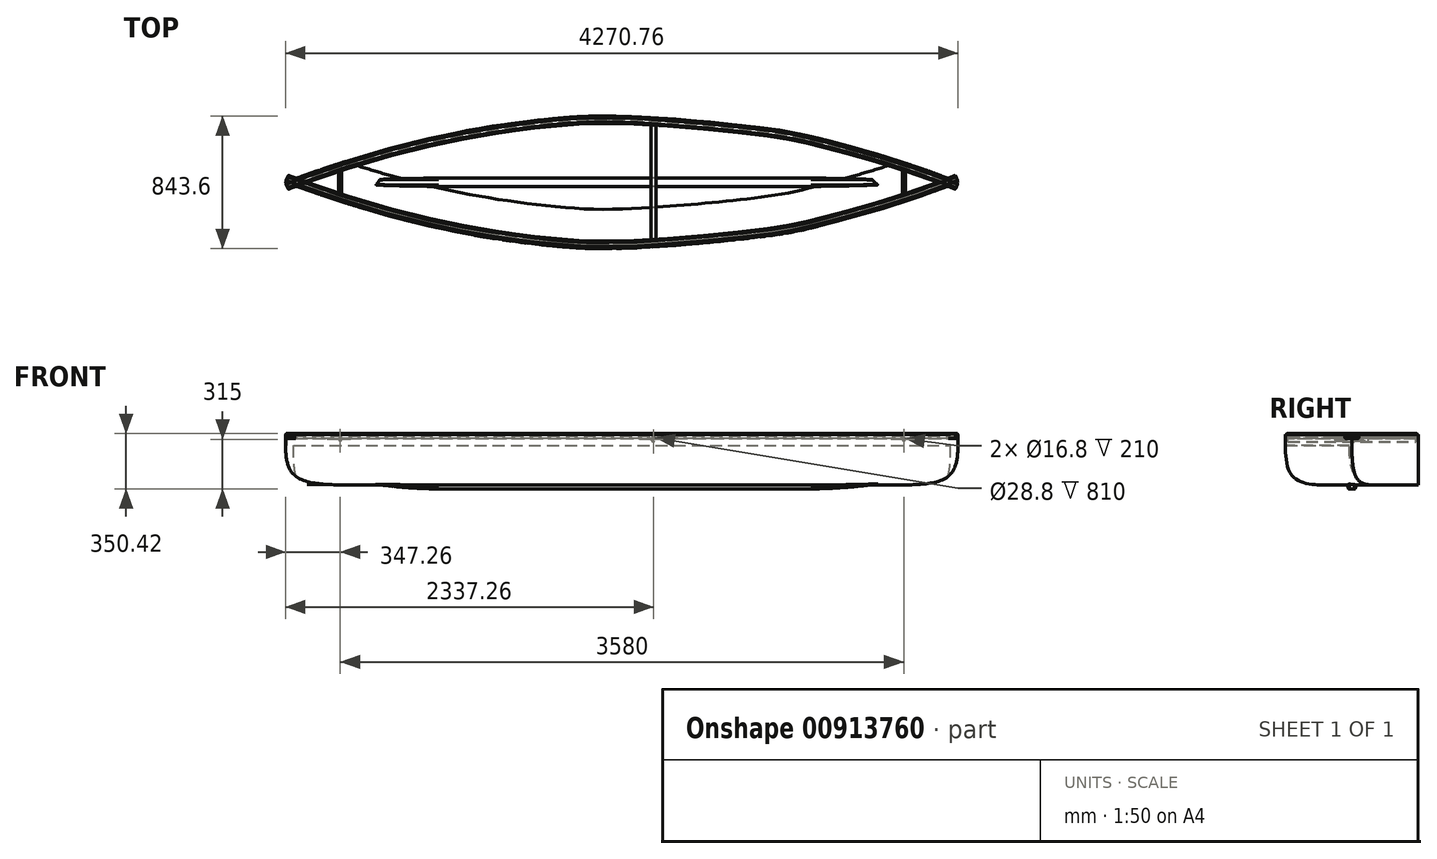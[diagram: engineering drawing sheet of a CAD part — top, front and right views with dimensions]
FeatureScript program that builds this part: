
annotation { "Feature Type Name" : "Feature", "Feature Type Description" : "" }
export const myFeature = defineFeature(function(context is Context, id is Id, definition is map)
    precondition{}
    {
        {
            var Q0;
            Q0=qCreatedBy(makeId("Top.planeOp"),FACE);
            var sketch = newSketch(context, id + "F0", { "sketchPlane" : qUnion([Q0])});
            skLineSegment(sketch, "E0", {"start": v(0, 0) * mm, "end": v(-3584.17, 0) * mm, "construction": true});
            skLineSegment(sketch, "E1", {"start": v(0, 0) * mm, "end": v(2133.5, 0) * mm, "construction": true});
            skFitSpline(sketch, "E2", {"points": [v(-2137.26, 0) * mm, v(-726.7, 370) * mm, v(-408.85, 407) * mm, v(0, 420) * mm, v(981, 333) * mm, v(1294.12, 267) * mm, v(2133.5, 0) * mm], "startDerivative": vector(8000.93, 3011.92) * mm, "endDerivative": vector(4907.5, -2014.73) * mm});
            skFitSpline(sketch, "E3.MirrorCS", {"points": [v(-2137.26, 0) * mm, v(-726.7, -370) * mm, v(-408.85, -407) * mm, v(0, -420) * mm, v(981, -333) * mm, v(1294.12, -267) * mm, v(2133.5, 0) * mm], "startDerivative": vector(8000.93, -3011.92) * mm, "endDerivative": vector(4907.5, 2014.73) * mm});
            skArc(sketch, "E4.filletArc", {"start": v(-2086.92, 18.76) * mm, "mid": v(-2100, 0) * mm, "end": v(-2086.92, -18.76) * mm});
            skArc(sketch, "E5.filletArc", {"start": v(2087.36, -18.6) * mm, "mid": v(2100, 0) * mm, "end": v(2087.36, 18.6) * mm});
            skSolve(sketch);
        }
        {
            var Q0;
            Q0 = qSketchRegion(id + "F0", true);
            extrude(context, id + "F1", {"entities" : qUnion([Q0]), "depth" : 320 * mm, "offsetDistance" : 25 * mm});
        }
        {
            var Q0;
            Q0=makeQuery(id+"F1.opExtrude","CAP_EDGE",EDGE,{"disambiguationData":[OSD([sQuery(id+"F0.wireOp",EDGE,"E3.MirrorCS")])],"isStart":true});
            fillet(context, id + "F2", {"entities" : qUnion([Q0]), "radius" : 250 * mm, "tangentPropagation" : true, "rho" : .6, "crossSection" : FilletCrossSection.CONIC, "allowEdgeOverflow" : false});
        }
        {
            var Q0;
            Q0=qCreatedBy(makeId("Right.planeOp"),FACE);
            var sketch = newSketch(context, id + "F3", { "sketchPlane" : qUnion([Q0])});
            skLineSegment(sketch, "E6", {"start": v(-27.5, 0) * mm, "end": v(-22.5, -25) * mm});
            skLineSegment(sketch, "E7", {"start": v(-22.5, -25) * mm, "end": v(22.5, -25) * mm});
            skLineSegment(sketch, "E8", {"start": v(22.5, -25) * mm, "end": v(27.5, 0) * mm});
            skLineSegment(sketch, "E9", {"start": v(27.5, 0) * mm, "end": v(-27.5, 0) * mm});
            skPoint(sketch, "E10.visualSharp", {"position": v(-22.5, -25) * mm});
            skPoint(sketch, "E11.visualSharp", {"position": v(22.5, -25) * mm});
            skSolve(sketch);
        }
        {
            var Q0;
            Q0 = qSketchRegion(id + "F3", true);
            extrude(context, id + "F4", {"entities" : qUnion([Q0]), "operationType" : NewBodyOperationType.ADD, "depth" : 1199.5 * mm, "offsetDistance" : 25 * mm, "hasSecondDirection" : true, "secondDirectionOppositeDirection" : true, "secondDirectionDepth" : 1166.8 * mm});
        }
        {
            var Q0;
            Q0=makeQuery(id+"F4.opExtrude","CAP_FACE",FACE,{"disambiguationData":[OSD([sQuery(id+"F3.wireOp",EDGE,"E6"),sQuery(id+"F3.wireOp",EDGE,"E7"),sQuery(id+"F3.wireOp",EDGE,"E8"),sQuery(id+"F3.wireOp",EDGE,"E9"),sQuery(id+"F3.wireOp",EDGE,"E10.filletArc"),sQuery(id+"F3.wireOp",EDGE,"E11.filletArc")])],"isStart":false});
            cPlane(context, id + "F5", {"entities" : qUnion([Q0]), "cplaneType" : CPlaneType.OFFSET, "offset" : 740 * mm, "width" : 150 * mm, "height" : 150 * mm});
        }
        {
            var Q0;
            Q0=qCreatedBy(id+"F5.planeOp",FACE);
            var sketch = newSketch(context, id + "F6", { "sketchPlane" : qUnion([Q0])});
            skLineSegment(sketch, "E12", {"start": v(-13, 52) * mm, "end": v(13, 52) * mm});
            skLineSegment(sketch, "E13", {"start": v(13, 52) * mm, "end": v(13.5, 57) * mm});
            skLineSegment(sketch, "E14", {"start": v(13.5, 57) * mm, "end": v(-13.5, 57) * mm});
            skLineSegment(sketch, "E15", {"start": v(-13.5, 57) * mm, "end": v(-13, 52) * mm});
            skSolve(sketch);
        }
        {
            var Q0;
            Q0=makeQuery(id+"F4.opExtrude","CAP_FACE",FACE,{"disambiguationData":[OSD([sQuery(id+"F3.wireOp",EDGE,"E6"),sQuery(id+"F3.wireOp",EDGE,"E7"),sQuery(id+"F3.wireOp",EDGE,"E8"),sQuery(id+"F3.wireOp",EDGE,"E9"),sQuery(id+"F3.wireOp",EDGE,"E10.filletArc"),sQuery(id+"F3.wireOp",EDGE,"E11.filletArc")])],"isStart":true});
            cPlane(context, id + "F7", {"entities" : qUnion([Q0]), "cplaneType" : CPlaneType.OFFSET, "offset" : 740 * mm, "width" : 150 * mm, "height" : 150 * mm});
        }
        {
            var Q0;
            Q0=makeQuery(id+"F2.opFillet","BLEND_EDGE",EDGE,{"disambiguationData":[OD(0.0)],"blendedFrom":[makeQuery(id+"F1.opExtrude","CAP_EDGE",EDGE,{"disambiguationData":[OSD([sQuery(id+"F0.wireOp",EDGE,"E2")])],"isStart":true}),makeQuery(id+"F1.opExtrude","CAP_EDGE",EDGE,{"disambiguationData":[OSD([sQuery(id+"F0.wireOp",EDGE,"E3.MirrorCS")])],"isStart":true})],"blendedInto":[]});
            var Q1;
            Q1=makeQuery(id+"F2.opFillet","BLEND_EDGE",EDGE,{"blendedFrom":[makeQuery(id+"F1.opExtrude","CAP_EDGE",EDGE,{"disambiguationData":[OSD([sQuery(id+"F0.wireOp",EDGE,"E3.MirrorCS")])],"isStart":true})],"blendedInto":[]});
            var Q3;
            Q3=makeQuery(id+"F4.opExtrude","CAP_FACE",FACE,{"disambiguationData":[OSD([sQuery(id+"F3.wireOp",EDGE,"E6"),sQuery(id+"F3.wireOp",EDGE,"E7"),sQuery(id+"F3.wireOp",EDGE,"E8"),sQuery(id+"F3.wireOp",EDGE,"E9")])],"isStart":false});
            var Q4;
            Q4 = qSketchRegion(id + "F6", true);
            var Q5;
            Q5=makeQuery(id+"F2.opFillet","BLEND_EDGE",EDGE,{"disambiguationData":[OD(0.0)],"blendedFrom":[makeQuery(id+"F1.opExtrude","CAP_EDGE",EDGE,{"disambiguationData":[OSD([sQuery(id+"F0.wireOp",EDGE,"E2")])],"isStart":true}),makeQuery(id+"F1.opExtrude","CAP_EDGE",EDGE,{"disambiguationData":[OSD([sQuery(id+"F0.wireOp",EDGE,"E3.MirrorCS")])],"isStart":true})],"blendedInto":[]});
            var Q6;
            Q6=makeQuery(id+"F2.opFillet","BLEND_EDGE",EDGE,{"blendedFrom":[makeQuery(id+"F1.opExtrude","CAP_EDGE",EDGE,{"disambiguationData":[OSD([sQuery(id+"F0.wireOp",EDGE,"E3.MirrorCS")])],"isStart":true})],"blendedInto":[]});
            var Q7;
            Q7=sQuery(id+"F6.wireOp",VERTEX,"E12.end");
            var Q8;
            Q8=makeQuery(id+"F4.opExtrude","CAP_VERTEX",VERTEX,{"disambiguationData":[OSD([sQuery(id+"F3.wireOp",EDGE,"E7"),sQuery(id+"F3.wireOp",EDGE,"E8")])],"isStart":false});
            loft(context, id + "F8", {"operationType" : NewBodyOperationType.ADD, "spine" : qUnion([Q0, Q1]), "startCondition" : LoftEndDerivativeType.MATCH_TANGENT, "startMagnitude" : 1, "sheetProfilesArray" : [{ "sheetProfileEntities" : qUnion([Q3]) }, { "sheetProfileEntities" : qUnion([Q4]) }], "guidesArray" : [{ "guideEntities" : qUnion([Q5]), "guideDerivativeType" : LoftGuideDerivativeType.DEFAULT, "guideDerivativeMagnitude" : 1 }, { "guideEntities" : qUnion([Q6]), "guideDerivativeType" : LoftGuideDerivativeType.DEFAULT, "guideDerivativeMagnitude" : 1 }], "matchConnections" : true, "connections" : [{ "connectionEntities" : qUnion([Q7, Q8]), "connectionEdgeQueries" : qUnion([]), "connectionEdgeParameters" : [] }]});
        }
        {
            var Q0;
            Q0=qCreatedBy(id+"F7.planeOp",FACE);
            var sketch = newSketch(context, id + "F9", { "sketchPlane" : qUnion([Q0])});
            skLineSegment(sketch, "E16", {"start": v(-14, 62) * mm, "end": v(14, 62) * mm});
            skLineSegment(sketch, "E17", {"start": v(14, 62) * mm, "end": v(13.5, 57) * mm});
            skLineSegment(sketch, "E18", {"start": v(13.5, 57) * mm, "end": v(-13.5, 57) * mm});
            skLineSegment(sketch, "E19", {"start": v(-13.5, 57) * mm, "end": v(-14, 62) * mm});
            skSolve(sketch);
        }
        {
            var Q1;
            Q1=makeQuery(id+"F9.imprint","IMPRINT",FACE,{"disambiguationData":[TD([[makeQuery(id+"F9.imprint","IMPRINT",EDGE,{"derivedFrom":sQuery(id+"F9.wireOp",EDGE,"E16")}),-1.0]])]});
            var Q2;
            Q2=makeQuery(id+"F4.opExtrude","CAP_FACE",FACE,{"disambiguationData":[OSD([sQuery(id+"F3.wireOp",EDGE,"E6"),sQuery(id+"F3.wireOp",EDGE,"E7"),sQuery(id+"F3.wireOp",EDGE,"E8"),sQuery(id+"F3.wireOp",EDGE,"E9"),sQuery(id+"F3.wireOp",EDGE,"E10.filletArc"),sQuery(id+"F3.wireOp",EDGE,"E11.filletArc")])],"isStart":true});
            loft(context, id + "F10", {"operationType" : NewBodyOperationType.ADD, "endCondition" : LoftEndDerivativeType.MATCH_TANGENT, "endMagnitude" : 1, "sheetProfilesArray" : [{ "sheetProfileEntities" : qUnion([Q1]) }, { "sheetProfileEntities" : qUnion([Q2]) }]});
        }
        {
            var Q0;
            Q0=makeQuery(id+"F8.opLoft","SWEPT_EDGE",EDGE,{"disambiguationData":[OSD([sQuery(id+"F3.wireOp",EDGE,"E7"),sQuery(id+"F3.wireOp",EDGE,"E8"),sQuery(id+"F6.wireOp",EDGE,"E12"),sQuery(id+"F6.wireOp",EDGE,"E13")])]});
            var Q1;
            Q1=makeQuery(id+"F4.opExtrude","SWEPT_EDGE",EDGE,{"disambiguationData":[OSD([sQuery(id+"F3.wireOp",EDGE,"E6"),sQuery(id+"F3.wireOp",EDGE,"E7")])]});
            fillet(context, id + "F11", {"entities" : qUnion([Q0, Q1]), "tangentPropagation" : true, "radius" : 5 * mm, "defaultsChanged" : false, "vertexSettings" : [], "allowEdgeOverflow" : false});
        }
        {
            var Q0;
            Q0=makeQuery(id+"F1.opExtrude","CAP_FACE",FACE,{"disambiguationData":[OSD([sQuery(id+"F0.wireOp",EDGE,"E2"),sQuery(id+"F0.wireOp",EDGE,"E3.MirrorCS"),sQuery(id+"F0.wireOp",EDGE,"E4.filletArc"),sQuery(id+"F0.wireOp",EDGE,"E5.filletArc")])],"isStart":false});
            shell(context, id + "F12", {"entities" : qUnion([Q0]), "thickness" : 2 * mm});
        }
        {
            var Q0;
            Q0=qCreatedBy(makeId("Right.planeOp"),FACE);
            var sketch = newSketch(context, id + "F13", { "sketchPlane" : qUnion([Q0])});
            skLineSegment(sketch, "E20", {"start": v(395.5, 293.42) * mm, "end": v(382.5, 293.42) * mm});
            skLineSegment(sketch, "E21", {"start": v(372.5, 303.42) * mm, "end": v(372.5, 315.42) * mm});
            skLineSegment(sketch, "E22", {"start": v(382.5, 325.42) * mm, "end": v(407.5, 325.42) * mm});
            skLineSegment(sketch, "E23", {"start": v(414.5, 318.42) * mm, "end": v(414.5, 318.42) * mm});
            skLineSegment(sketch, "E24", {"start": v(407.5, 311.42) * mm, "end": v(407.5, 311.42) * mm});
            skLineSegment(sketch, "E25", {"start": v(402.5, 306.42) * mm, "end": v(402.5, 293.42) * mm});
            skLineSegment(sketch, "E26", {"start": v(397.5, 295.42) * mm, "end": v(397.5, 320.92) * mm});
            skLineSegment(sketch, "E27.0", {"start": v(375, 303.92) * mm, "end": v(375, 314.92) * mm});
            skLineSegment(sketch, "E27.1", {"start": v(393, 295.92) * mm, "end": v(383, 295.92) * mm});
            skLineSegment(sketch, "E27.2", {"start": v(395, 297.92) * mm, "end": v(395, 320.92) * mm});
            skLineSegment(sketch, "E28.0", {"start": v(400, 306.94) * mm, "end": v(400, 293.42) * mm});
            skLineSegment(sketch, "E28.3", {"start": v(383, 322.92) * mm, "end": v(393, 322.92) * mm});
            skLineSegment(sketch, "E29", {"start": v(400, 293.42) * mm, "end": v(402.5, 293.42) * mm});
            skLineSegment(sketch, "E30.trimOffspring", {"start": v(399.5, 322.92) * mm, "end": v(407.98, 322.92) * mm});
            skPoint(sketch, "E31.visualSharp", {"position": v(372.5, 325.42) * mm});
            skArc(sketch, "E31.filletArc", {"start": v(382.5, 325.42) * mm, "mid": v(375.43, 322.5) * mm, "end": v(372.5, 315.42) * mm});
            skPoint(sketch, "E32.visualSharp", {"position": v(414.5, 325.42) * mm});
            skArc(sketch, "E32.filletArc", {"start": v(414.5, 318.42) * mm, "mid": v(412.45, 323.37) * mm, "end": v(407.5, 325.42) * mm});
            skPoint(sketch, "E33.visualSharp", {"position": v(414.5, 311.42) * mm});
            skArc(sketch, "E33.filletArc", {"start": v(407.5, 311.42) * mm, "mid": v(412.45, 313.47) * mm, "end": v(414.5, 318.42) * mm});
            skPoint(sketch, "E34.visualSharp", {"position": v(402.5, 311.42) * mm});
            skArc(sketch, "E34.filletArc", {"start": v(407.5, 311.42) * mm, "mid": v(403.96, 309.96) * mm, "end": v(402.5, 306.42) * mm});
            skPoint(sketch, "E35.visualSharp", {"position": v(372.5, 293.42) * mm});
            skArc(sketch, "E35.filletArc", {"start": v(372.5, 303.42) * mm, "mid": v(375.43, 296.35) * mm, "end": v(382.5, 293.42) * mm});
            skPoint(sketch, "E36.visualSharp", {"position": v(397.5, 293.42) * mm});
            skArc(sketch, "E36.filletArc", {"start": v(395.5, 293.42) * mm, "mid": v(396.91, 294) * mm, "end": v(397.5, 295.42) * mm});
            skPoint(sketch, "E37.visualSharp", {"position": v(397.5, 322.92) * mm});
            skArc(sketch, "E37.filletArc", {"start": v(399.5, 322.92) * mm, "mid": v(398.09, 322.34) * mm, "end": v(397.5, 320.92) * mm});
            skPoint(sketch, "E38.visualSharp", {"position": v(395, 322.92) * mm});
            skArc(sketch, "E38.filletArc", {"start": v(395, 320.92) * mm, "mid": v(394.41, 322.34) * mm, "end": v(393, 322.92) * mm});
            skPoint(sketch, "E39.visualSharp", {"position": v(375, 322.92) * mm});
            skArc(sketch, "E39.filletArc", {"start": v(383, 322.92) * mm, "mid": v(377.34, 320.58) * mm, "end": v(375, 314.92) * mm});
            skPoint(sketch, "E40.visualSharp", {"position": v(375, 295.92) * mm});
            skArc(sketch, "E40.filletArc", {"start": v(375, 303.92) * mm, "mid": v(377.34, 298.27) * mm, "end": v(383, 295.92) * mm});
            skPoint(sketch, "E41.visualSharp", {"position": v(395, 295.92) * mm});
            skArc(sketch, "E41.filletArc", {"start": v(393, 295.92) * mm, "mid": v(394.41, 296.5) * mm, "end": v(395, 297.92) * mm});
            skPoint(sketch, "E42.visualSharp", {"position": v(400, 313.75) * mm});
            skArc(sketch, "E42.filletArc", {"start": v(407, 313.94) * mm, "mid": v(402.05, 311.9) * mm, "end": v(400, 306.94) * mm});
            skPoint(sketch, "E43.visualSharp", {"position": v(412, 322.92) * mm});
            skArc(sketch, "E43.filletArc", {"start": v(411.98, 318.92) * mm, "mid": v(410.8, 321.75) * mm, "end": v(407.98, 322.92) * mm});
            skPoint(sketch, "E44.visualSharp", {"position": v(412, 313.75) * mm});
            skLineSegment(sketch, "E45.0", {"start": v(407.5, 313.94) * mm, "end": v(407, 313.94) * mm});
            skArc(sketch, "E45.1", {"start": v(407.5, 313.94) * mm, "mid": v(410.67, 315.25) * mm, "end": v(411.98, 318.42) * mm});
            skLineSegment(sketch, "E45.2", {"start": v(411.98, 318.92) * mm, "end": v(411.98, 318.42) * mm});
            skSolve(sketch);
        }
        {
            var Q0;
            Q0=makeQuery(id+"F13.imprint","IMPRINT",FACE,{"disambiguationData":[TD([[makeQuery(id+"F13.imprint","IMPRINT",EDGE,{"derivedFrom":sQuery(id+"F13.wireOp",EDGE,"E20")}),-1.0]])]});
            var Q1;
            Q1=sQuery(id+"F13.wireOp",EDGE,"E31.filletArc");
            var Q2;
            Q2=sQuery(id+"F13.wireOp",EDGE,"E35.filletArc");
            var Q3;
            Q3=sQuery(id+"F13.wireOp",EDGE,"E21");
            var Q4;
            Q4=sQuery(id+"F13.wireOp",EDGE,"E20");
            var Q5;
            Q5=sQuery(id+"F13.wireOp",EDGE,"E36.filletArc");
            var Q6;
            Q6=sQuery(id+"F13.wireOp",EDGE,"E26");
            var Q7;
            Q7=sQuery(id+"F13.wireOp",EDGE,"E37.filletArc");
            var Q8;
            Q8=sQuery(id+"F13.wireOp",EDGE,"E30.trimOffspring");
            var Q9;
            Q9=sQuery(id+"F13.wireOp",EDGE,"E22");
            var Q10;
            Q10=sQuery(id+"F13.wireOp",EDGE,"E32.filletArc");
            var Q11;
            Q11=sQuery(id+"F13.wireOp",EDGE,"E43.filletArc");
            var Q12;
            Q12=sQuery(id+"F13.wireOp",EDGE,"E33.filletArc");
            var Q13;
            Q13=sQuery(id+"F13.wireOp",EDGE,"E34.filletArc");
            var Q14;
            Q14=sQuery(id+"F13.wireOp",EDGE,"E25");
            var Q15;
            Q15=sQuery(id+"F13.wireOp",EDGE,"E29");
            var Q16;
            Q16=sQuery(id+"F13.wireOp",EDGE,"E28.0");
            var Q17;
            Q17=sQuery(id+"F13.wireOp",EDGE,"E42.filletArc");
            var Q18;
            Q18=sQuery(id+"F13.wireOp",EDGE,"E27.2");
            var Q19;
            Q19=sQuery(id+"F13.wireOp",EDGE,"E38.filletArc");
            var Q20;
            Q20=sQuery(id+"F13.wireOp",EDGE,"E28.3");
            var Q21;
            Q21=sQuery(id+"F13.wireOp",EDGE,"E39.filletArc");
            var Q22;
            Q22=sQuery(id+"F13.wireOp",EDGE,"E27.0");
            var Q23;
            Q23=sQuery(id+"F13.wireOp",EDGE,"E40.filletArc");
            var Q24;
            Q24=sQuery(id+"F13.wireOp",EDGE,"E27.1");
            var Q25;
            Q25=sQuery(id+"F13.wireOp",EDGE,"E41.filletArc");
            var Q26;
            Q26=makeQuery(id+"F1.opExtrude","CAP_EDGE",EDGE,{"disambiguationData":[OSD([sQuery(id+"F0.wireOp",EDGE,"E2")])],"isStart":false});
            sweep(context, id + "F14", {"profiles" : qUnion([Q0]), "surfaceProfiles" : qUnion([Q1, Q2, Q3, Q4, Q5, Q6, Q7, Q8, Q9, Q10, Q11, Q12, Q13, Q14, Q15, Q16, Q17, Q18, Q19, Q20, Q21, Q22, Q23, Q24, Q25]), "path" : qUnion([Q26])});
        }
        {
            var Q0;
            Q0=makeQuery(id+"F14.opSweep","SWEPT_BODY",BODY,{"disambiguationData":[OSD([sQuery(id+"F0.wireOp",EDGE,"E2"),sQuery(id+"F13.wireOp",EDGE,"E20"),sQuery(id+"F13.wireOp",EDGE,"E21"),sQuery(id+"F13.wireOp",EDGE,"E22"),sQuery(id+"F13.wireOp",EDGE,"E25"),sQuery(id+"F13.wireOp",EDGE,"E26"),sQuery(id+"F13.wireOp",EDGE,"E27.0"),sQuery(id+"F13.wireOp",EDGE,"E27.1"),sQuery(id+"F13.wireOp",EDGE,"E27.2"),sQuery(id+"F13.wireOp",EDGE,"E28.0"),sQuery(id+"F13.wireOp",EDGE,"E28.3"),sQuery(id+"F13.wireOp",EDGE,"E29"),sQuery(id+"F13.wireOp",EDGE,"E30.trimOffspring"),sQuery(id+"F13.wireOp",EDGE,"E31.filletArc"),sQuery(id+"F13.wireOp",EDGE,"E32.filletArc"),sQuery(id+"F13.wireOp",EDGE,"E33.filletArc"),sQuery(id+"F13.wireOp",EDGE,"E34.filletArc"),sQuery(id+"F13.wireOp",EDGE,"E35.filletArc"),sQuery(id+"F13.wireOp",EDGE,"E36.filletArc"),sQuery(id+"F13.wireOp",EDGE,"E37.filletArc"),sQuery(id+"F13.wireOp",EDGE,"E38.filletArc"),sQuery(id+"F13.wireOp",EDGE,"E39.filletArc"),sQuery(id+"F13.wireOp",EDGE,"E40.filletArc"),sQuery(id+"F13.wireOp",EDGE,"E41.filletArc"),sQuery(id+"F13.wireOp",EDGE,"E42.filletArc"),sQuery(id+"F13.wireOp",EDGE,"E43.filletArc"),sQuery(id+"F13.wireOp",EDGE,"E45.0"),sQuery(id+"F13.wireOp",EDGE,"E45.1"),sQuery(id+"F13.wireOp",EDGE,"E45.2")])]});
            var Q1;
            Q1=qCreatedBy(makeId("Front.planeOp"),FACE);
            mirror(context, id + "F15", {"entities" : qUnion([Q0]), "mirrorPlane" : qUnion([Q1])});
        }
        {
            var Q0;
            Q0=makeQuery(id+"F1.opExtrude","CAP_FACE",FACE,{"disambiguationData":[OSD([sQuery(id+"F0.wireOp",EDGE,"E2"),sQuery(id+"F0.wireOp",EDGE,"E3.MirrorCS"),sQuery(id+"F0.wireOp",EDGE,"E4.filletArc"),sQuery(id+"F0.wireOp",EDGE,"E5.filletArc")])],"isStart":false});
            var sketch = newSketch(context, id + "F16", { "sketchPlane" : qUnion([Q0])});
            skCircle(sketch, "E46", {"center": v(-2098, 0) * mm, "radius": 0.5 * mm});
            skCircle(sketch, "E47", {"center": v(-405.85, 405.26) * mm, "radius": 0.5 * mm});
            skCircle(sketch, "E48", {"center": v(1290.64, 265.84) * mm, "radius": 0.5 * mm});
            skCircle(sketch, "E49", {"center": v(0, 418) * mm, "radius": 0.5 * mm});
            skCircle(sketch, "E50", {"center": v(2098, 0) * mm, "radius": 0.5 * mm});
            skSolve(sketch);
        }
        {
            var Q0;
            Q0 = qSketchRegion(id + "F16", true);
            extrude(context, id + "F17", {"entities" : qUnion([Q0]), "operationType" : NewBodyOperationType.ADD, "depth" : 1 * mm, "offsetDistance" : 25 * mm});
        }
        {
            var Q0;
            Q0=qCreatedBy(makeId("Front.planeOp"),FACE);
            var sketch = newSketch(context, id + "F18", { "sketchPlane" : qUnion([Q0])});
            skCircle(sketch, "E51", {"center": v(200, 290) * mm, "radius": 16 * mm});
            skCircle(sketch, "E52.0", {"center": v(200, 290) * mm, "radius": 14.4 * mm});
            skSolve(sketch);
        }
        {
            var Q0;
            Q0 = qSketchRegion(id + "F18", true);
            extrude(context, id + "F19", {"entities" : qUnion([Q0]), "endBound" : BoundingType.SYMMETRIC, "depth" : 810 * mm, "offsetDistance" : 25 * mm});
        }
        {
            var Q0;
            Q0=qCreatedBy(makeId("Front.planeOp"),FACE);
            var sketch = newSketch(context, id + "F20", { "sketchPlane" : qUnion([Q0])});
            skCircle(sketch, "E53", {"center": v(-1790, 290) * mm, "radius": 10 * mm});
            skCircle(sketch, "E54.0", {"center": v(-1790, 290) * mm, "radius": 8.4 * mm});
            skLineSegment(sketch, "E55", {"start": v(0, 0) * mm, "end": v(0, 23.84) * mm, "construction": true});
            skLineSegment(sketch, "E56", {"start": v(0, 23.84) * mm, "end": v(0, 0) * mm});
            skCircle(sketch, "E57.MirrorC", {"center": v(1790, 290) * mm, "radius": 10 * mm});
            skCircle(sketch, "E58.MirrorC", {"center": v(1790, 290) * mm, "radius": 8.4 * mm});
            skSolve(sketch);
        }
        {
            var Q0;
            Q0 = qSketchRegion(id + "F20", true);
            extrude(context, id + "F21", {"entities" : qUnion([Q0]), "endBound" : BoundingType.SYMMETRIC, "depth" : 210 * mm, "offsetDistance" : 25 * mm});
        }
    });
